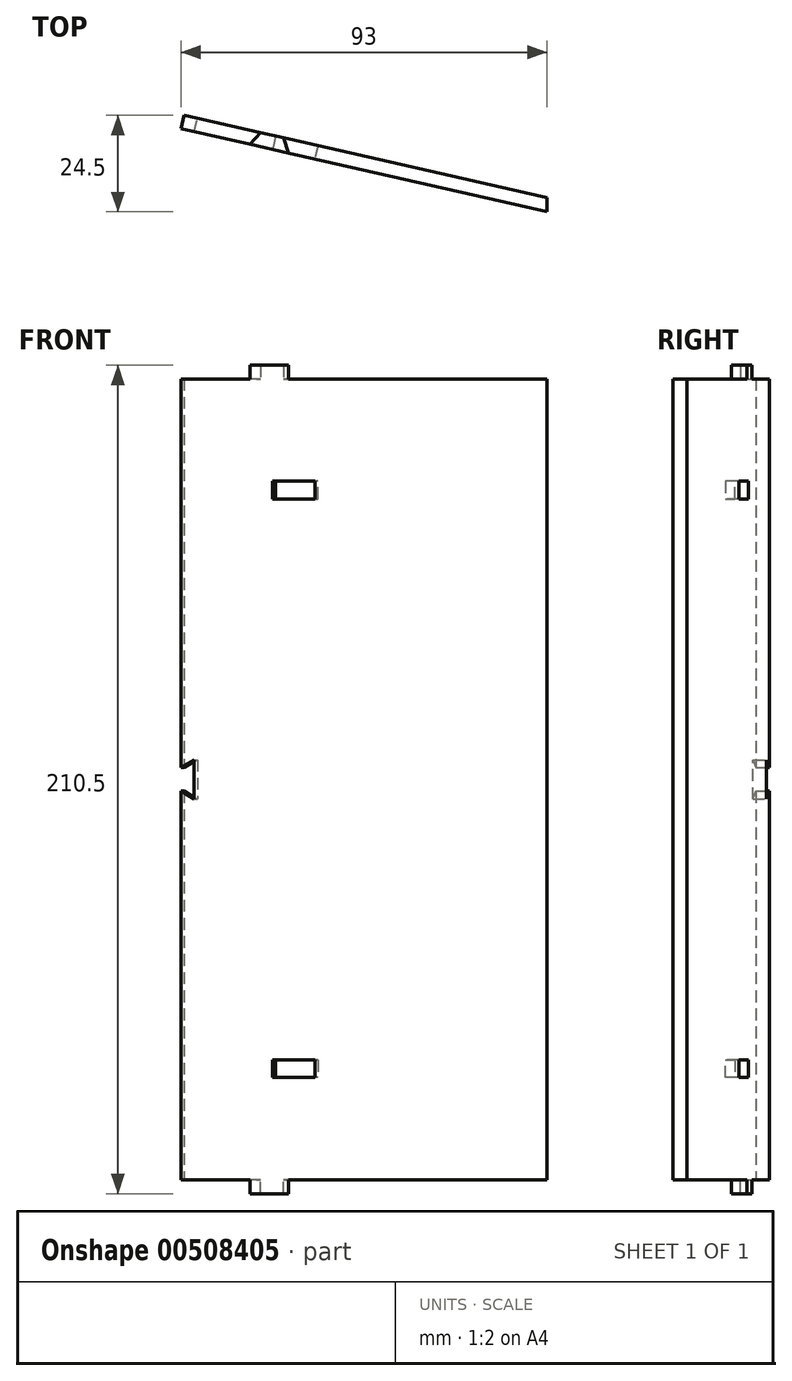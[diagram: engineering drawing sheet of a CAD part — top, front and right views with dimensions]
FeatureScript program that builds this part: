
annotation { "Feature Type Name" : "Feature", "Feature Type Description" : "" }
export const myFeature = defineFeature(function(context is Context, id is Id, definition is map)
    precondition{}
    {
        {
            var Q0;
            Q0=qCreatedBy(makeId("Top.planeOp"),FACE);
            var sketch = newSketch(context, id + "F0", { "sketchPlane" : qUnion([Q0])});
            skLineSegment(sketch, "E0", {"start": v(24.84, -18.93) * mm, "end": v(-50.16, -18.93) * mm});
            skLineSegment(sketch, "E1", {"start": v(24.84, -18.93) * mm, "end": v(99.84, -18.93) * mm});
            skLineSegment(sketch, "E2", {"start": v(99.84, -18.93) * mm, "end": v(110.34, -18.93) * mm});
            skLineSegment(sketch, "E3", {"start": v(-50.16, 17.46) * mm, "end": v(-50.16, -18.93) * mm});
            skLineSegment(sketch, "E4", {"start": v(110.34, -18.93) * mm, "end": v(-50.16, 17.46) * mm});
            skLineSegment(sketch, "E5", {"start": v(110.34, -18.93) * mm, "end": v(80.34, -18.93) * mm});
            skLineSegment(sketch, "E6", {"start": v(80.34, -18.93) * mm, "end": v(-50.16, -18.93) * mm});
            skLineSegment(sketch, "E7", {"start": v(-50.16, 21.05) * mm, "end": v(-50.16, 17.46) * mm});
            skLineSegment(sketch, "E8", {"start": v(-50.16, 21.05) * mm, "end": v(110.34, -15.34) * mm});
            skLineSegment(sketch, "E9", {"start": v(110.34, -15.34) * mm, "end": v(110.34, -18.93) * mm});
            skLineSegment(sketch, "E10", {"start": v(80.34, -18.93) * mm, "end": v(80.34, -12.13) * mm});
            skLineSegment(sketch, "E11", {"start": v(-50.16, -18.93) * mm, "end": v(80.34, -18.93) * mm});
            skLineSegment(sketch, "E12", {"start": v(-50.16, -18.93) * mm, "end": v(-46.66, -18.93) * mm});
            skLineSegment(sketch, "E13", {"start": v(-46.66, -18.93) * mm, "end": v(-46.66, 16.67) * mm});
            skLineSegment(sketch, "E14", {"start": v(-46.66, 16.67) * mm, "end": v(-50.16, 16.67) * mm});
            skLineSegment(sketch, "E15", {"start": v(-46.66, 16.67) * mm, "end": v(-46.66, 20.26) * mm});
            skLineSegment(sketch, "E16", {"start": v(-46.66, 16.67) * mm, "end": v(-45.88, 20.08) * mm});
            skLineSegment(sketch, "E17", {"start": v(-50.16, 21.05) * mm, "end": v(-46.66, 21.05) * mm});
            skLineSegment(sketch, "E18", {"start": v(-46.66, 21.05) * mm, "end": v(-46.66, 20.26) * mm});
            skLineSegment(sketch, "E19", {"start": v(-50.16, 17.46) * mm, "end": v(-50.93, 17.64) * mm});
            skLineSegment(sketch, "E20", {"start": v(-50.93, 17.64) * mm, "end": v(-50.16, 21.05) * mm});
            skLineSegment(sketch, "E21", {"start": v(-50.16, 17.46) * mm, "end": v(18.1, 1.98) * mm});
            skLineSegment(sketch, "E22", {"start": v(18.1, 5.57) * mm, "end": v(17.34, 2.16) * mm});
            skSolve(sketch);
        }
        {
            var Q0;
            {var subQ0=sQuery(id+"F0.wireOp",EDGE,"E9");Q0=makeQuery(id+"F0.imprint","IMPRINT",FACE,{"disambiguationData":[TD([[makeQuery(id+"F0.imprint","IMPRINT",EDGE,{"derivedFrom":subQ0}),-1.0]])]});}
            extrude(context, id + "F1", {"entities" : qUnion([Q0]), "depth" : 203.5 * mm, "offsetDistance" : 25 * mm});
        }
        {
            var Q0;
            Q0=makeQuery(id+"F1.opExtrude","CAP_FACE",FACE,{"disambiguationData":[OSD([sQuery(id+"F0.wireOp",EDGE,"E4"),sQuery(id+"F0.wireOp",EDGE,"E8"),sQuery(id+"F0.wireOp",EDGE,"E9"),sQuery(id+"F0.wireOp",EDGE,"E21"),sQuery(id+"F0.wireOp",EDGE,"E22")])],"isStart":false});
            var sketch = newSketch(context, id + "F2", { "sketchPlane" : qUnion([Q0])});
            skLineSegment(sketch, "E23", {"start": v(18.1, 5.57) * mm, "end": v(37.61, 1.15) * mm});
            skLineSegment(sketch, "E24", {"start": v(37.61, 1.15) * mm, "end": v(43.47, -0.18) * mm});
            skLineSegment(sketch, "E25", {"start": v(17.34, 2.16) * mm, "end": v(34.89, -1.82) * mm});
            skLineSegment(sketch, "E26", {"start": v(34.89, -1.82) * mm, "end": v(44.64, -4.03) * mm});
            skLineSegment(sketch, "E27", {"start": v(44.64, -4.03) * mm, "end": v(43.47, -0.18) * mm});
            skLineSegment(sketch, "E28", {"start": v(37.61, 1.15) * mm, "end": v(34.89, -1.82) * mm});
            skLineSegment(sketch, "E29", {"start": v(110.34, -15.34) * mm, "end": v(109.57, -18.76) * mm});
            skLineSegment(sketch, "E30", {"start": v(109.57, -18.76) * mm, "end": v(92.01, -14.78) * mm});
            skLineSegment(sketch, "E31", {"start": v(92.01, -14.78) * mm, "end": v(82.26, -12.56) * mm});
            skLineSegment(sketch, "E32", {"start": v(110.34, -15.34) * mm, "end": v(90.84, -10.92) * mm});
            skLineSegment(sketch, "E33", {"start": v(90.84, -10.92) * mm, "end": v(84.99, -9.6) * mm});
            skLineSegment(sketch, "E34", {"start": v(84.99, -9.6) * mm, "end": v(82.26, -12.56) * mm});
            skLineSegment(sketch, "E35", {"start": v(92.01, -14.78) * mm, "end": v(90.84, -10.92) * mm});
            skSolve(sketch);
        }
        {
            var Q0;
            Q0=makeQuery(id+"F2.imprint","IMPRINT",FACE,{"disambiguationData":[TD([[makeQuery(id+"F2.imprint","IMPRINT",EDGE,{"derivedFrom":sQuery(id+"F2.wireOp",EDGE,"E24")}),-1.0]])]});
            var Q1;
            Q1=makeQuery(id+"F2.imprint","IMPRINT",FACE,{"disambiguationData":[TD([[makeQuery(id+"F2.imprint","IMPRINT",EDGE,{"derivedFrom":sQuery(id+"F2.wireOp",EDGE,"E31")}),1.0]])]});
            extrude(context, id + "F3", {"entities" : qUnion([Q0, Q1]), "operationType" : NewBodyOperationType.ADD, "depth" : 3.5 * mm, "offsetDistance" : 25 * mm});
        }
        {
            var Q0;
            Q0=makeQuery(id+"F3.opExtrude","CAP_FACE",FACE,{"disambiguationData":[OSD([sQuery(id+"F2.wireOp",EDGE,"E24"),sQuery(id+"F2.wireOp",EDGE,"E26"),sQuery(id+"F2.wireOp",EDGE,"E27"),sQuery(id+"F2.wireOp",EDGE,"E28")])],"isStart":false});
            var Q1;
            Q1=makeQuery(id+"F3.opExtrude","CAP_FACE",FACE,{"disambiguationData":[OSD([sQuery(id+"F2.wireOp",EDGE,"E31"),sQuery(id+"F2.wireOp",EDGE,"E33"),sQuery(id+"F2.wireOp",EDGE,"E34"),sQuery(id+"F2.wireOp",EDGE,"E35")])],"isStart":false});
            extrude(context, id + "F4", {"entities" : qUnion([Q0, Q1]), "operationType" : NewBodyOperationType.ADD, "oppositeDirection" : true, "depth" : 210.5 * mm, "offsetDistance" : 25 * mm});
        }
        {
            var Q0;
            {var subQ0=sQuery(id+"F2.wireOp",EDGE,"E33");var subQ1=sQuery(id+"F2.wireOp",EDGE,"E24");Q0=makeQuery(id+"F4.boolean.opBoolean","MERGE",FACE,{"derivedFrom":[makeQuery(id+"F3.boolean.opBoolean","MERGE",FACE,{"derivedFrom":[makeQuery(id+"F1.opExtrude","SWEPT_FACE",FACE,{"disambiguationData":[OSD([sQuery(id+"F0.wireOp",EDGE,"E8")])]}),makeQuery(id+"F3.opExtrude","SWEPT_FACE",FACE,{"disambiguationData":[OSD([subQ1])]}),makeQuery(id+"F3.opExtrude","SWEPT_FACE",FACE,{"disambiguationData":[OSD([subQ0])]})]}),makeQuery(id+"F4.opExtrude","SWEPT_FACE",FACE,{"disambiguationData":[OSD([subQ1])]}),makeQuery(id+"F4.opExtrude","SWEPT_FACE",FACE,{"disambiguationData":[OSD([subQ0])]})]});}
            var sketch = newSketch(context, id + "F5", { "sketchPlane" : qUnion([Q0])});
            skLineSegment(sketch, "E36", {"start": v(-16.43, 203.5) * mm, "end": v(-19.93, 203.5) * mm});
            skLineSegment(sketch, "E37", {"start": v(-19.93, 203.5) * mm, "end": v(-19.93, 0) * mm});
            skLineSegment(sketch, "E38", {"start": v(-19.93, 0) * mm, "end": v(-19.93, 25) * mm});
            skLineSegment(sketch, "E39", {"start": v(-19.93, 25) * mm, "end": v(-19.93, 35) * mm});
            skLineSegment(sketch, "E40", {"start": v(-19.93, 35) * mm, "end": v(-19.93, 101.75) * mm});
            skLineSegment(sketch, "E41", {"start": v(-19.93, 101.75) * mm, "end": v(-19.93, 96.75) * mm});
            skLineSegment(sketch, "E42", {"start": v(-19.93, 96.75) * mm, "end": v(-19.93, 106.75) * mm});
            skLineSegment(sketch, "E43", {"start": v(-19.93, 203.5) * mm, "end": v(-19.93, 178.5) * mm});
            skLineSegment(sketch, "E44", {"start": v(-19.93, 178.5) * mm, "end": v(-19.93, 168.5) * mm});
            skLineSegment(sketch, "E45", {"start": v(-16.43, 203.5) * mm, "end": v(-16.43, 176.5) * mm});
            skLineSegment(sketch, "E46", {"start": v(-16.43, 176.5) * mm, "end": v(-16.43, 170.5) * mm});
            skLineSegment(sketch, "E47", {"start": v(-16.43, 101.75) * mm, "end": v(-16.43, 104.75) * mm});
            skLineSegment(sketch, "E48", {"start": v(-16.43, 104.75) * mm, "end": v(-16.43, 98.75) * mm});
            skLineSegment(sketch, "E49", {"start": v(-16.43, 98.75) * mm, "end": v(-19.93, 96.75) * mm});
            skLineSegment(sketch, "E50", {"start": v(-16.43, 104.75) * mm, "end": v(-19.93, 106.75) * mm});
            skLineSegment(sketch, "E51", {"start": v(-16.43, 0) * mm, "end": v(-16.43, 27) * mm});
            skLineSegment(sketch, "E52", {"start": v(-16.43, 27) * mm, "end": v(-16.43, 33) * mm});
            skLineSegment(sketch, "E53", {"start": v(-16.43, 33) * mm, "end": v(-19.93, 35) * mm});
            skLineSegment(sketch, "E54", {"start": v(-16.43, 27) * mm, "end": v(-19.93, 25) * mm});
            skLineSegment(sketch, "E55", {"start": v(-19.93, 168.5) * mm, "end": v(-16.43, 170.5) * mm});
            skLineSegment(sketch, "E56", {"start": v(-16.43, 176.5) * mm, "end": v(-19.93, 178.5) * mm});
            skSolve(sketch);
        }
        {
            var Q0;
            Q0=makeQuery(id+"F5.imprint","IMPRINT",FACE,{"disambiguationData":[TD([[makeQuery(id+"F5.imprint","IMPRINT",EDGE,{"derivedFrom":sQuery(id+"F5.wireOp",EDGE,"E44")}),1.0]])]});
            var Q1;
            {var subQ0=sQuery(id+"F5.wireOp",EDGE,"E49");Q1=makeQuery(id+"F5.imprint","IMPRINT",FACE,{"disambiguationData":[TD([[makeQuery(id+"F5.imprint","IMPRINT",EDGE,{"derivedFrom":subQ0}),-1.0]])]});}
            var Q2;
            Q2=makeQuery(id+"F5.imprint","IMPRINT",FACE,{"disambiguationData":[TD([[makeQuery(id+"F5.imprint","IMPRINT",EDGE,{"derivedFrom":sQuery(id+"F5.wireOp",EDGE,"E39")}),-1.0]])]});
            extrude(context, id + "F6", {"entities" : qUnion([Q0, Q1, Q2]), "operationType" : NewBodyOperationType.REMOVE, "oppositeDirection" : true, "depth" : 25 * mm, "offsetDistance" : 25 * mm});
        }
        {
            var Q0;
            {var subQ0=sQuery(id+"F2.wireOp",EDGE,"E31");var subQ1=sQuery(id+"F2.wireOp",EDGE,"E26");Q0=makeQuery(id+"F4.boolean.opBoolean","MERGE",FACE,{"derivedFrom":[makeQuery(id+"F3.boolean.opBoolean","MERGE",FACE,{"derivedFrom":[makeQuery(id+"F1.opExtrude","SWEPT_FACE",FACE,{"disambiguationData":[OSD([sQuery(id+"F0.wireOp",EDGE,"E4"),sQuery(id+"F0.wireOp",EDGE,"E21")])]}),makeQuery(id+"F3.opExtrude","SWEPT_FACE",FACE,{"disambiguationData":[OSD([subQ1])]}),makeQuery(id+"F3.opExtrude","SWEPT_FACE",FACE,{"disambiguationData":[OSD([subQ0])]})]}),makeQuery(id+"F4.opExtrude","SWEPT_FACE",FACE,{"disambiguationData":[OSD([subQ1])]}),makeQuery(id+"F4.opExtrude","SWEPT_FACE",FACE,{"disambiguationData":[OSD([subQ0])]})]});}
            var sketch = newSketch(context, id + "F7", { "sketchPlane" : qUnion([Q0])});
            skLineSegment(sketch, "E57", {"start": v(16.43, 0) * mm, "end": v(16.43, 26) * mm});
            skLineSegment(sketch, "E58", {"start": v(16.43, 26) * mm, "end": v(40.81, 26) * mm});
            skLineSegment(sketch, "E59", {"start": v(40.81, 26) * mm, "end": v(50.81, 26) * mm});
            skLineSegment(sketch, "E60", {"start": v(50.81, 26) * mm, "end": v(50.81, 30.5) * mm});
            skLineSegment(sketch, "E61", {"start": v(50.81, 30.5) * mm, "end": v(40.81, 30.5) * mm});
            skLineSegment(sketch, "E62", {"start": v(40.81, 30.5) * mm, "end": v(40.81, 26) * mm});
            skLineSegment(sketch, "E63", {"start": v(40.81, 30.5) * mm, "end": v(40.81, 173) * mm});
            skLineSegment(sketch, "E64", {"start": v(40.81, 173) * mm, "end": v(40.81, 177.5) * mm});
            skLineSegment(sketch, "E65", {"start": v(40.81, 177.5) * mm, "end": v(50.81, 177.5) * mm});
            skLineSegment(sketch, "E66", {"start": v(50.81, 177.5) * mm, "end": v(50.81, 173) * mm});
            skLineSegment(sketch, "E67", {"start": v(50.81, 173) * mm, "end": v(40.81, 173) * mm});
            skSolve(sketch);
        }
        {
            var Q0;
            Q0=makeQuery(id+"F7.imprint","IMPRINT",FACE,{"disambiguationData":[TD([[makeQuery(id+"F7.imprint","IMPRINT",EDGE,{"derivedFrom":sQuery(id+"F7.wireOp",EDGE,"E64")}),-1.0]])]});
            var Q1;
            Q1=makeQuery(id+"F7.imprint","IMPRINT",FACE,{"disambiguationData":[TD([[makeQuery(id+"F7.imprint","IMPRINT",EDGE,{"derivedFrom":sQuery(id+"F7.wireOp",EDGE,"E59")}),1.0]])]});
            extrude(context, id + "F8", {"entities" : qUnion([Q0, Q1]), "operationType" : NewBodyOperationType.REMOVE, "oppositeDirection" : true, "depth" : 25 * mm, "offsetDistance" : 25 * mm});
        }
        {
            var Q0;
            Q0=makeQuery(id+"F8.boolean.opBoolean","COPY",FACE,{"derivedFrom":makeQuery(id+"F8.opExtrude","SWEPT_FACE",FACE,{"disambiguationData":[OSD([sQuery(id+"F7.wireOp",EDGE,"E64")])]})});
            var Q1;
            Q1=makeQuery(id+"F8.boolean.opBoolean","COPY",FACE,{"derivedFrom":makeQuery(id+"F8.opExtrude","SWEPT_FACE",FACE,{"disambiguationData":[OSD([sQuery(id+"F7.wireOp",EDGE,"E62")])]})});
            extrude(context, id + "F9", {"entities" : qUnion([Q0, Q1]), "operationType" : NewBodyOperationType.REMOVE, "oppositeDirection" : true, "depth" : .5 * mm, "offsetDistance" : 25 * mm});
        }
        {
            var Q0;
            Q0=makeQuery(id+"F8.boolean.opBoolean","COPY",FACE,{"derivedFrom":makeQuery(id+"F8.opExtrude","SWEPT_FACE",FACE,{"disambiguationData":[OSD([sQuery(id+"F7.wireOp",EDGE,"E66")])]})});
            var Q1;
            Q1=makeQuery(id+"F8.boolean.opBoolean","COPY",FACE,{"derivedFrom":makeQuery(id+"F8.opExtrude","SWEPT_FACE",FACE,{"disambiguationData":[OSD([sQuery(id+"F7.wireOp",EDGE,"E60")])]})});
            extrude(context, id + "F10", {"entities" : qUnion([Q0, Q1]), "operationType" : NewBodyOperationType.REMOVE, "oppositeDirection" : true, "depth" : .5 * mm, "offsetDistance" : 25 * mm});
        }
    });
